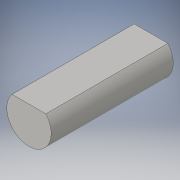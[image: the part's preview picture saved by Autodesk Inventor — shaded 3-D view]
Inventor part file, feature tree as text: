
AUTODESK INVENTOR PART (.ipt)
format: ipt  version: 2016 SP1 (Build 200210100, 210)  size: 86,016 bytes
history: native  units: in
note: dims shown in document units (in); Inventor stores cm internally (conversion verified against a paired STEP export)
features: other x3, sketch x1
ambient origin geometry x8: Origin, YZ Plane, XZ Plane, XY Plane, X Axis, Y Axis, Z Axis, Center Point
bodies: Solid1 (feature_tree)
feature tree (4):
  other  "Motor Shaft.ipt"
  other  "Solid1::Motor Shaft.ipt"
  other  "TaggingFeature1"
  sketch  "Sketch1"  dims[d0=0.3937in]
